annotation { "Feature Type Name" : "Feature", "Feature Type Description" : "" }
export const myFeature = defineFeature(function(context is Context, id is Id, definition is map)
    precondition{}
    {
        {
            var Q0;
            Q0=qCreatedBy(makeId("Top.planeOp"),FACE);
            var sketch = newSketch(context, id + "F0", { "sketchPlane" : qUnion([Q0])});
            skLineSegment(sketch, "E0.bottom", {"start": v(58.42, -33.26) * mm, "end": v(-58.42, -33.26) * mm});
            skLineSegment(sketch, "E0.top", {"start": v(58.42, -7.86) * mm, "end": v(-58.42, -7.86) * mm});
            skLineSegment(sketch, "E0.left", {"start": v(58.42, -33.26) * mm, "end": v(58.42, -7.86) * mm});
            skLineSegment(sketch, "E0.right", {"start": v(-58.42, -33.26) * mm, "end": v(-58.42, -7.86) * mm});
            skPoint(sketch, "E0.middle", {"position": v(0, -20.56) * mm});
            skSolve(sketch);
        }
        {
            var Q0;
            Q0=qCreatedBy(makeId("Front.planeOp"),FACE);
            var sketch = newSketch(context, id + "F1", { "sketchPlane" : qUnion([Q0])});
            skCircle(sketch, "E1", {"center": v(0, 0) * mm, "radius": 6.35 * mm});
            skCircle(sketch, "E2", {"center": v(0, 0) * mm, "radius": 7.62 * mm});
            skLineSegment(sketch, "E3", {"start": v(0, 0) * mm, "end": v(15.24, 0) * mm, "construction": true});
            skCircle(sketch, "E4", {"center": v(15.24, 0) * mm, "radius": 7.62 * mm});
            skCircle(sketch, "E5", {"center": v(15.24, 0) * mm, "radius": 6.35 * mm});
            skLineSegment(sketch, "E6", {"start": v(15.24, 0) * mm, "end": v(30.48, 0) * mm, "construction": true});
            skCircle(sketch, "E7", {"center": v(30.48, 0) * mm, "radius": 7.62 * mm});
            skCircle(sketch, "E8", {"center": v(30.48, 0) * mm, "radius": 6.35 * mm});
            skLineSegment(sketch, "E9", {"start": v(0, 0) * mm, "end": v(-15.24, 0) * mm, "construction": true});
            skCircle(sketch, "E10", {"center": v(-15.24, 0) * mm, "radius": 7.62 * mm});
            skCircle(sketch, "E11", {"center": v(-15.24, 0) * mm, "radius": 6.35 * mm});
            skLineSegment(sketch, "E12", {"start": v(-15.24, 0) * mm, "end": v(-30.48, 0) * mm, "construction": true});
            skCircle(sketch, "E13", {"center": v(-30.48, 0) * mm, "radius": 7.62 * mm});
            skCircle(sketch, "E14", {"center": v(-30.48, 0) * mm, "radius": 6.35 * mm});
            skLineSegment(sketch, "E15", {"start": v(-30.48, 0) * mm, "end": v(-45.72, 0) * mm, "construction": true});
            skCircle(sketch, "E16", {"center": v(-45.72, 0) * mm, "radius": 7.62 * mm});
            skCircle(sketch, "E17", {"center": v(-45.72, 0) * mm, "radius": 6.35 * mm});
            skLineSegment(sketch, "E18", {"start": v(30.48, 0) * mm, "end": v(45.72, 0) * mm, "construction": true});
            skCircle(sketch, "E19", {"center": v(45.72, 0) * mm, "radius": 7.62 * mm});
            skCircle(sketch, "E20", {"center": v(45.72, 0) * mm, "radius": 6.35 * mm});
            skLineSegment(sketch, "E21.bottom", {"start": v(-37.46, -1.27) * mm, "end": v(-38.73, -1.27) * mm, "construction": true});
            skLineSegment(sketch, "E21.top", {"start": v(-37.46, 1.27) * mm, "end": v(-38.73, 1.27) * mm, "construction": true});
            skLineSegment(sketch, "E21.left", {"start": v(-37.46, -1.27) * mm, "end": v(-37.46, 1.27) * mm, "construction": true});
            skLineSegment(sketch, "E21.right", {"start": v(-38.73, -1.27) * mm, "end": v(-38.73, 1.27) * mm, "construction": true});
            skPoint(sketch, "E21.middle", {"position": v(-38.1, 0) * mm});
            skLineSegment(sketch, "E22.1.0.0", {"start": v(-23.5, -1.27) * mm, "end": v(-23.5, 1.27) * mm, "construction": true});
            skLineSegment(sketch, "E22.1.0.1", {"start": v(-22.22, -1.27) * mm, "end": v(-23.5, -1.27) * mm, "construction": true});
            skLineSegment(sketch, "E22.1.0.2", {"start": v(-22.22, -1.27) * mm, "end": v(-22.22, 1.27) * mm, "construction": true});
            skLineSegment(sketch, "E22.1.0.3", {"start": v(-22.22, 1.27) * mm, "end": v(-23.5, 1.27) * mm, "construction": true});
            skLineSegment(sketch, "E22.2.0.0", {"start": v(-8.25, -1.27) * mm, "end": v(-8.25, 1.27) * mm, "construction": true});
            skLineSegment(sketch, "E22.2.0.1", {"start": v(-6.98, -1.27) * mm, "end": v(-8.25, -1.27) * mm, "construction": true});
            skLineSegment(sketch, "E22.2.0.2", {"start": v(-6.98, -1.27) * mm, "end": v(-6.98, 1.27) * mm, "construction": true});
            skLineSegment(sketch, "E22.2.0.3", {"start": v(-6.98, 1.27) * mm, "end": v(-8.25, 1.27) * mm, "construction": true});
            skLineSegment(sketch, "E22.3.0.0", {"start": v(6.99, -1.27) * mm, "end": v(6.99, 1.27) * mm, "construction": true});
            skLineSegment(sketch, "E22.3.0.1", {"start": v(8.26, -1.27) * mm, "end": v(6.99, -1.27) * mm, "construction": true});
            skLineSegment(sketch, "E22.3.0.2", {"start": v(8.26, -1.27) * mm, "end": v(8.26, 1.27) * mm, "construction": true});
            skLineSegment(sketch, "E22.3.0.3", {"start": v(8.26, 1.27) * mm, "end": v(6.99, 1.27) * mm, "construction": true});
            skLineSegment(sketch, "E22.4.0.0", {"start": v(22.23, -1.27) * mm, "end": v(22.23, 1.27) * mm, "construction": true});
            skLineSegment(sketch, "E22.4.0.1", {"start": v(23.5, -1.27) * mm, "end": v(22.23, -1.27) * mm, "construction": true});
            skLineSegment(sketch, "E22.4.0.2", {"start": v(23.5, -1.27) * mm, "end": v(23.5, 1.27) * mm, "construction": true});
            skLineSegment(sketch, "E22.4.0.3", {"start": v(23.5, 1.27) * mm, "end": v(22.23, 1.27) * mm, "construction": true});
            skLineSegment(sketch, "E22.5.0.0", {"start": v(37.47, -1.27) * mm, "end": v(37.47, 1.27) * mm, "construction": true});
            skLineSegment(sketch, "E22.5.0.1", {"start": v(38.74, -1.27) * mm, "end": v(37.47, -1.27) * mm, "construction": true});
            skLineSegment(sketch, "E22.5.0.2", {"start": v(38.74, -1.27) * mm, "end": v(38.74, 1.27) * mm, "construction": true});
            skLineSegment(sketch, "E22.5.0.3", {"start": v(38.74, 1.27) * mm, "end": v(37.47, 1.27) * mm, "construction": true});
            skSolve(sketch);
        }
        {
            var Q0;
            Q0=qCreatedBy(makeId("Front.planeOp"),FACE);
            var sketch = newSketch(context, id + "F2", { "sketchPlane" : qUnion([Q0])});
            skLineSegment(sketch, "E23", {"start": v(0, 0) * mm, "end": v(-38.1, 0) * mm, "construction": true});
            skPoint(sketch, "E24", {"position": v(-38.1, 0) * mm});
            skLineSegment(sketch, "E25.bottom", {"start": v(-37.46, -1.27) * mm, "end": v(-38.73, -1.27) * mm});
            skLineSegment(sketch, "E25.top", {"start": v(-37.46, 1.27) * mm, "end": v(-38.73, 1.27) * mm});
            skLineSegment(sketch, "E25.left", {"start": v(-37.46, -1.27) * mm, "end": v(-37.46, 1.27) * mm});
            skLineSegment(sketch, "E25.right", {"start": v(-38.73, -1.27) * mm, "end": v(-38.73, 1.27) * mm});
            skLineSegment(sketch, "E26.1.0.0", {"start": v(-22.22, 1.27) * mm, "end": v(-23.5, 1.27) * mm});
            skLineSegment(sketch, "E26.1.0.1", {"start": v(-23.5, -1.27) * mm, "end": v(-23.5, 1.27) * mm});
            skLineSegment(sketch, "E26.1.0.2", {"start": v(-22.22, -1.27) * mm, "end": v(-23.5, -1.27) * mm});
            skLineSegment(sketch, "E26.1.0.3", {"start": v(-22.22, -1.27) * mm, "end": v(-22.22, 1.27) * mm});
            skLineSegment(sketch, "E26.2.0.0", {"start": v(-6.98, 1.27) * mm, "end": v(-8.25, 1.27) * mm});
            skLineSegment(sketch, "E26.2.0.1", {"start": v(-8.25, -1.27) * mm, "end": v(-8.25, 1.27) * mm});
            skLineSegment(sketch, "E26.2.0.2", {"start": v(-6.98, -1.27) * mm, "end": v(-8.25, -1.27) * mm});
            skLineSegment(sketch, "E26.2.0.3", {"start": v(-6.98, -1.27) * mm, "end": v(-6.98, 1.27) * mm});
            skLineSegment(sketch, "E26.3.0.0", {"start": v(8.25, 1.27) * mm, "end": v(6.98, 1.27) * mm});
            skLineSegment(sketch, "E26.3.0.1", {"start": v(6.98, -1.27) * mm, "end": v(6.98, 1.27) * mm});
            skLineSegment(sketch, "E26.3.0.2", {"start": v(8.25, -1.27) * mm, "end": v(6.98, -1.27) * mm});
            skLineSegment(sketch, "E26.3.0.3", {"start": v(8.25, -1.27) * mm, "end": v(8.25, 1.27) * mm});
            skLineSegment(sketch, "E26.4.0.0", {"start": v(23.5, 1.27) * mm, "end": v(22.23, 1.27) * mm});
            skLineSegment(sketch, "E26.4.0.1", {"start": v(22.23, -1.27) * mm, "end": v(22.23, 1.27) * mm});
            skLineSegment(sketch, "E26.4.0.2", {"start": v(23.5, -1.27) * mm, "end": v(22.23, -1.27) * mm});
            skLineSegment(sketch, "E26.4.0.3", {"start": v(23.5, -1.27) * mm, "end": v(23.5, 1.27) * mm});
            skLineSegment(sketch, "E26.5.0.0", {"start": v(38.74, 1.27) * mm, "end": v(37.47, 1.27) * mm});
            skLineSegment(sketch, "E26.5.0.1", {"start": v(37.47, -1.27) * mm, "end": v(37.47, 1.27) * mm});
            skLineSegment(sketch, "E26.5.0.2", {"start": v(38.74, -1.27) * mm, "end": v(37.47, -1.27) * mm});
            skLineSegment(sketch, "E26.5.0.3", {"start": v(38.74, -1.27) * mm, "end": v(38.74, 1.27) * mm});
            skLineSegment(sketch, "E26.direction1", {"start": v(-38.73, 1.27) * mm, "end": v(-23.5, 1.27) * mm, "construction": true});
            skLineSegment(sketch, "E27", {"start": v(0, 0) * mm, "end": v(0, 6.35) * mm});
            skLineSegment(sketch, "E28", {"start": v(0, 6.35) * mm, "end": v(-47.71, 6.35) * mm});
            skSolve(sketch);
        }
        {
            var Q0;
            Q0=makeQuery(id+"F1.imprint","IMPRINT",FACE,{"disambiguationData":[TD([[makeQuery(id+"F1.imprint","IMPRINT",EDGE,{"derivedFrom":sQuery(id+"F1.wireOp",EDGE,"E17")}),-1.0]])]});
            extrude(context, id + "F3", {"entities" : qUnion([Q0]), "oppositeDirection" : true, "depth" : -152.4 * mm, "offsetDistance" : 25.4 * mm});
        }
        {
            var Q0;
            Q0 = qSketchRegion(id + "F0", true);
            extrude(context, id + "F4", {"entities" : qUnion([Q0]), "operationType" : NewBodyOperationType.ADD, "endBound" : BoundingType.SYMMETRIC, "depth" : 25.4 * mm, "offsetDistance" : 25.4 * mm});
        }
        {
            var Q0;
            Q0=makeQuery(id+"F2.imprint","IMPRINT",FACE,{"disambiguationData":[TD([[makeQuery(id+"F2.imprint","IMPRINT",EDGE,{"derivedFrom":sQuery(id+"F2.wireOp",EDGE,"E25.bottom")}),-1.0]])]});
            extrude(context, id + "F5", {"entities" : qUnion([Q0]), "operationType" : NewBodyOperationType.ADD, "depth" : 127 * mm, "offsetDistance" : 25.4 * mm});
        }
        {
            var Q0;
            Q0=makeQuery(id+"F1.imprint","IMPRINT",FACE,{"disambiguationData":[TD([[makeQuery(id+"F1.imprint","IMPRINT",EDGE,{"derivedFrom":sQuery(id+"F1.wireOp",EDGE,"E14")}),-1.0]])]});
            extrude(context, id + "F6", {"entities" : qUnion([Q0]), "operationType" : NewBodyOperationType.ADD, "depth" : 127 * mm, "offsetDistance" : 25.4 * mm});
        }
        {
            var Q0;
            Q0=makeQuery(id+"F2.imprint","IMPRINT",FACE,{"disambiguationData":[TD([[makeQuery(id+"F2.imprint","IMPRINT",EDGE,{"derivedFrom":sQuery(id+"F2.wireOp",EDGE,"E26.1.0.0")}),1.0]])]});
            extrude(context, id + "F7", {"entities" : qUnion([Q0]), "operationType" : NewBodyOperationType.ADD, "oppositeDirection" : true, "depth" : -101.6 * mm, "offsetDistance" : 25.4 * mm});
        }
        {
            var Q0;
            Q0=makeQuery(id+"F1.imprint","IMPRINT",FACE,{"disambiguationData":[TD([[makeQuery(id+"F1.imprint","IMPRINT",EDGE,{"derivedFrom":sQuery(id+"F1.wireOp",EDGE,"E11")}),-1.0]])]});
            extrude(context, id + "F8", {"entities" : qUnion([Q0]), "operationType" : NewBodyOperationType.ADD, "depth" : 101.6 * mm, "offsetDistance" : 25.4 * mm});
        }
        {
            var Q0;
            Q0=makeQuery(id+"F2.imprint","IMPRINT",FACE,{"disambiguationData":[TD([[makeQuery(id+"F2.imprint","IMPRINT",EDGE,{"derivedFrom":sQuery(id+"F2.wireOp",EDGE,"E26.2.0.0")}),1.0]])]});
            extrude(context, id + "F9", {"entities" : qUnion([Q0]), "operationType" : NewBodyOperationType.ADD, "depth" : 76.2 * mm, "offsetDistance" : 25.4 * mm});
        }
        {
            var Q0;
            Q0=makeQuery(id+"F1.imprint","IMPRINT",FACE,{"disambiguationData":[TD([[makeQuery(id+"F1.imprint","IMPRINT",EDGE,{"derivedFrom":sQuery(id+"F1.wireOp",EDGE,"E1")}),-1.0]])]});
            extrude(context, id + "F10", {"entities" : qUnion([Q0]), "operationType" : NewBodyOperationType.ADD, "depth" : 76.2 * mm, "offsetDistance" : 25.4 * mm});
        }
        {
            var Q0;
            Q0=makeQuery(id+"F2.imprint","IMPRINT",FACE,{"disambiguationData":[TD([[makeQuery(id+"F2.imprint","IMPRINT",EDGE,{"derivedFrom":sQuery(id+"F2.wireOp",EDGE,"E26.3.0.0")}),1.0]])]});
            extrude(context, id + "F11", {"entities" : qUnion([Q0]), "operationType" : NewBodyOperationType.ADD, "depth" : 63.5 * mm, "offsetDistance" : 25.4 * mm});
        }
        {
            var Q0;
            Q0=makeQuery(id+"F1.imprint","IMPRINT",FACE,{"disambiguationData":[TD([[makeQuery(id+"F1.imprint","IMPRINT",EDGE,{"derivedFrom":sQuery(id+"F1.wireOp",EDGE,"E5")}),-1.0]])]});
            extrude(context, id + "F12", {"entities" : qUnion([Q0]), "operationType" : NewBodyOperationType.ADD, "depth" : 63.5 * mm, "offsetDistance" : 25.4 * mm});
        }
        {
            var Q0;
            Q0=makeQuery(id+"F2.imprint","IMPRINT",FACE,{"disambiguationData":[TD([[makeQuery(id+"F2.imprint","IMPRINT",EDGE,{"derivedFrom":sQuery(id+"F2.wireOp",EDGE,"E26.4.0.0")}),1.0]])]});
            extrude(context, id + "F13", {"entities" : qUnion([Q0]), "operationType" : NewBodyOperationType.ADD, "depth" : 50.8 * mm, "offsetDistance" : 25.4 * mm});
        }
        {
            var Q0;
            Q0=makeQuery(id+"F1.imprint","IMPRINT",FACE,{"disambiguationData":[TD([[makeQuery(id+"F1.imprint","IMPRINT",EDGE,{"derivedFrom":sQuery(id+"F1.wireOp",EDGE,"E8")}),-1.0]])]});
            extrude(context, id + "F14", {"entities" : qUnion([Q0]), "operationType" : NewBodyOperationType.ADD, "depth" : 50.8 * mm, "offsetDistance" : 25.4 * mm});
        }
        {
            var Q0;
            Q0=makeQuery(id+"F2.imprint","IMPRINT",FACE,{"disambiguationData":[TD([[makeQuery(id+"F2.imprint","IMPRINT",EDGE,{"derivedFrom":sQuery(id+"F2.wireOp",EDGE,"E26.5.0.0")}),1.0]])]});
            extrude(context, id + "F15", {"entities" : qUnion([Q0]), "operationType" : NewBodyOperationType.ADD, "depth" : 38.1 * mm, "offsetDistance" : 25.4 * mm});
        }
        {
            var Q0;
            Q0=makeQuery(id+"F1.imprint","IMPRINT",FACE,{"disambiguationData":[TD([[makeQuery(id+"F1.imprint","IMPRINT",EDGE,{"derivedFrom":sQuery(id+"F1.wireOp",EDGE,"E20")}),-1.0]])]});
            extrude(context, id + "F16", {"entities" : qUnion([Q0]), "operationType" : NewBodyOperationType.ADD, "depth" : 38.1 * mm, "offsetDistance" : 25.4 * mm});
        }
        {
            var Q0;
            Q0=makeQuery(id+"F4.boolean.opBoolean","SPLIT",FACE,{"disambiguationData":[TD([makeQuery(id+"F3.opExtrude","SWEPT_FACE",FACE,{"disambiguationData":[OSD([sQuery(id+"F1.wireOp",EDGE,"E17")])]})])],"derivedFrom":makeQuery(id+"F4.opExtrude","SWEPT_FACE",FACE,{"disambiguationData":[OSD([sQuery(id+"F0.wireOp",EDGE,"E0.top")])]})});
            var Q1;
            {var subQ2=sQuery(id+"F0.wireOp",EDGE,"E0.top");Q1=makeQuery(id+"F6.boolean.opBoolean","SPLIT",FACE,{"disambiguationData":[TD([makeQuery(id+"F6.opExtrude","SWEPT_FACE",FACE,{"disambiguationData":[OSD([sQuery(id+"F1.wireOp",EDGE,"E14")])]})])],"derivedFrom":makeQuery(id+"F4.boolean.opBoolean","SPLIT",FACE,{"disambiguationData":[TD([makeQuery(id+"F3.opExtrude","SWEPT_FACE",FACE,{"disambiguationData":[OSD([sQuery(id+"F1.wireOp",EDGE,"E16")])]})])],"derivedFrom":makeQuery(id+"F4.opExtrude","SWEPT_FACE",FACE,{"disambiguationData":[OSD([subQ2])]})})});}
            var Q2;
            {var subQ2=sQuery(id+"F0.wireOp",EDGE,"E0.top");var subQ7=makeQuery(id+"F3.opExtrude","SWEPT_FACE",FACE,{"disambiguationData":[OSD([sQuery(id+"F1.wireOp",EDGE,"E16")])]});Q2=makeQuery(id+"F8.boolean.opBoolean","SPLIT",FACE,{"disambiguationData":[TD([makeQuery(id+"F8.opExtrude","SWEPT_FACE",FACE,{"disambiguationData":[OSD([sQuery(id+"F1.wireOp",EDGE,"E11")])]})])],"derivedFrom":makeQuery(id+"F6.boolean.opBoolean","SPLIT",FACE,{"disambiguationData":[TD([subQ7])],"derivedFrom":makeQuery(id+"F4.boolean.opBoolean","SPLIT",FACE,{"disambiguationData":[TD([subQ7])],"derivedFrom":makeQuery(id+"F4.opExtrude","SWEPT_FACE",FACE,{"disambiguationData":[OSD([subQ2])]})})})});}
            var Q3;
            {var subQ5=makeQuery(id+"F3.opExtrude","SWEPT_FACE",FACE,{"disambiguationData":[OSD([sQuery(id+"F1.wireOp",EDGE,"E16")])]});var subQ8=sQuery(id+"F0.wireOp",EDGE,"E0.top");Q3=makeQuery(id+"F10.boolean.opBoolean","SPLIT",FACE,{"disambiguationData":[TD([makeQuery(id+"F10.opExtrude","SWEPT_FACE",FACE,{"disambiguationData":[OSD([sQuery(id+"F1.wireOp",EDGE,"E1")])]})])],"derivedFrom":makeQuery(id+"F8.boolean.opBoolean","SPLIT",FACE,{"disambiguationData":[TD([subQ5])],"derivedFrom":makeQuery(id+"F6.boolean.opBoolean","SPLIT",FACE,{"disambiguationData":[TD([subQ5])],"derivedFrom":makeQuery(id+"F4.boolean.opBoolean","SPLIT",FACE,{"disambiguationData":[TD([subQ5])],"derivedFrom":makeQuery(id+"F4.opExtrude","SWEPT_FACE",FACE,{"disambiguationData":[OSD([subQ8])]})})})})});}
            var Q4;
            {var subQ6=makeQuery(id+"F3.opExtrude","SWEPT_FACE",FACE,{"disambiguationData":[OSD([sQuery(id+"F1.wireOp",EDGE,"E16")])]});var subQ9=sQuery(id+"F0.wireOp",EDGE,"E0.top");Q4=makeQuery(id+"F12.boolean.opBoolean","SPLIT",FACE,{"disambiguationData":[TD([makeQuery(id+"F12.opExtrude","SWEPT_FACE",FACE,{"disambiguationData":[OSD([sQuery(id+"F1.wireOp",EDGE,"E5")])]})])],"derivedFrom":makeQuery(id+"F10.boolean.opBoolean","SPLIT",FACE,{"disambiguationData":[TD([subQ6])],"derivedFrom":makeQuery(id+"F8.boolean.opBoolean","SPLIT",FACE,{"disambiguationData":[TD([subQ6])],"derivedFrom":makeQuery(id+"F6.boolean.opBoolean","SPLIT",FACE,{"disambiguationData":[TD([subQ6])],"derivedFrom":makeQuery(id+"F4.boolean.opBoolean","SPLIT",FACE,{"disambiguationData":[TD([subQ6])],"derivedFrom":makeQuery(id+"F4.opExtrude","SWEPT_FACE",FACE,{"disambiguationData":[OSD([subQ9])]})})})})})});}
            var Q5;
            {var subQ7=makeQuery(id+"F3.opExtrude","SWEPT_FACE",FACE,{"disambiguationData":[OSD([sQuery(id+"F1.wireOp",EDGE,"E16")])]});var subQ10=sQuery(id+"F0.wireOp",EDGE,"E0.top");Q5=makeQuery(id+"F14.boolean.opBoolean","SPLIT",FACE,{"disambiguationData":[TD([makeQuery(id+"F14.opExtrude","SWEPT_FACE",FACE,{"disambiguationData":[OSD([sQuery(id+"F1.wireOp",EDGE,"E8")])]})])],"derivedFrom":makeQuery(id+"F12.boolean.opBoolean","SPLIT",FACE,{"disambiguationData":[TD([subQ7])],"derivedFrom":makeQuery(id+"F10.boolean.opBoolean","SPLIT",FACE,{"disambiguationData":[TD([subQ7])],"derivedFrom":makeQuery(id+"F8.boolean.opBoolean","SPLIT",FACE,{"disambiguationData":[TD([subQ7])],"derivedFrom":makeQuery(id+"F6.boolean.opBoolean","SPLIT",FACE,{"disambiguationData":[TD([subQ7])],"derivedFrom":makeQuery(id+"F4.boolean.opBoolean","SPLIT",FACE,{"disambiguationData":[TD([subQ7])],"derivedFrom":makeQuery(id+"F4.opExtrude","SWEPT_FACE",FACE,{"disambiguationData":[OSD([subQ10])]})})})})})})});}
            var Q6;
            {var subQ7=makeQuery(id+"F3.opExtrude","SWEPT_FACE",FACE,{"disambiguationData":[OSD([sQuery(id+"F1.wireOp",EDGE,"E16")])]});var subQ10=sQuery(id+"F0.wireOp",EDGE,"E0.top");Q6=makeQuery(id+"F16.boolean.opBoolean","SPLIT",FACE,{"disambiguationData":[TD([makeQuery(id+"F16.opExtrude","SWEPT_FACE",FACE,{"disambiguationData":[OSD([sQuery(id+"F1.wireOp",EDGE,"E20")])]})])],"derivedFrom":makeQuery(id+"F14.boolean.opBoolean","SPLIT",FACE,{"disambiguationData":[TD([subQ7])],"derivedFrom":makeQuery(id+"F12.boolean.opBoolean","SPLIT",FACE,{"disambiguationData":[TD([subQ7])],"derivedFrom":makeQuery(id+"F10.boolean.opBoolean","SPLIT",FACE,{"disambiguationData":[TD([subQ7])],"derivedFrom":makeQuery(id+"F8.boolean.opBoolean","SPLIT",FACE,{"disambiguationData":[TD([subQ7])],"derivedFrom":makeQuery(id+"F6.boolean.opBoolean","SPLIT",FACE,{"disambiguationData":[TD([subQ7])],"derivedFrom":makeQuery(id+"F4.boolean.opBoolean","SPLIT",FACE,{"disambiguationData":[TD([subQ7])],"derivedFrom":makeQuery(id+"F4.opExtrude","SWEPT_FACE",FACE,{"disambiguationData":[OSD([subQ10])]})})})})})})})});}
            extrude(context, id + "F17", {"entities" : qUnion([Q0, Q1, Q2, Q3, Q4, Q5, Q6]), "operationType" : NewBodyOperationType.REMOVE, "oppositeDirection" : true, "depth" : 152.4 * mm, "offsetDistance" : 25.4 * mm});
        }
        {
            var Q0;
            Q0=makeQuery(id+"F4.opExtrude","CAP_FACE",FACE,{"disambiguationData":[OSD([sQuery(id+"F0.wireOp",EDGE,"E0.bottom"),sQuery(id+"F0.wireOp",EDGE,"E0.top"),sQuery(id+"F0.wireOp",EDGE,"E0.left"),sQuery(id+"F0.wireOp",EDGE,"E0.right")])],"isStart":false});
            var sketch = newSketch(context, id + "F18", { "sketchPlane" : qUnion([Q0])});
            skLineSegment(sketch, "E29.bottom", {"start": v(53.34, -26.94) * mm, "end": v(-53.34, -26.94) * mm});
            skLineSegment(sketch, "E29.top", {"start": v(53.34, -14.18) * mm, "end": v(-53.34, -14.18) * mm});
            skLineSegment(sketch, "E29.left", {"start": v(53.34, -26.94) * mm, "end": v(53.34, -14.18) * mm});
            skLineSegment(sketch, "E29.right", {"start": v(-53.34, -26.94) * mm, "end": v(-53.34, -14.18) * mm});
            skPoint(sketch, "E29.middle", {"position": v(0, -20.56) * mm});
            skText(sketch, "E30", { "text": "Jake Powers", "fontName": "RobotoSlab-Regular.ttf"});
            const initialGuessF18  = {"E30": [-0.05334, -0.02694, 1, 0, 0.01275]};
            skSetInitialGuess(sketch, initialGuessF18);
            skSolve(sketch);
        }
        {
            var Q0;
            Q0=makeQuery(id+"F18.imprint","IMPRINT",FACE,{"disambiguationData":[TD([[makeQuery(id+"F18.imprint","IMPRINT",EDGE,{"derivedFrom":sQuery(id+"F18.wireOp",EDGE,"E30.sketch_text.stroke-0")}),-1.0]])]});
            var Q1;
            Q1=makeQuery(id+"F18.imprint","IMPRINT",FACE,{"disambiguationData":[TD([[makeQuery(id+"F18.imprint","IMPRINT",EDGE,{"derivedFrom":sQuery(id+"F18.wireOp",EDGE,"E30.sketch_text.stroke-18")}),-1.0]])]});
            var Q2;
            {var subQ0=sQuery(id+"F18.wireOp",EDGE,"E30.sketch_text.stroke-56");Q2=makeQuery(id+"F18.imprint","IMPRINT",FACE,{"disambiguationData":[TD([[makeQuery(id+"F18.imprint","IMPRINT",EDGE,{"derivedFrom":subQ0}),-1.0]])]});}
            var Q3;
            {var subQ4=sQuery(id+"F18.wireOp",EDGE,"E30.sketch_text.stroke-81");Q3=makeQuery(id+"F18.imprint","IMPRINT",FACE,{"disambiguationData":[TD([[makeQuery(id+"F18.imprint","IMPRINT",EDGE,{"derivedFrom":subQ4}),-1.0]])]});}
            var Q4;
            Q4=makeQuery(id+"F18.imprint","IMPRINT",FACE,{"disambiguationData":[TD([[makeQuery(id+"F18.imprint","IMPRINT",EDGE,{"derivedFrom":sQuery(id+"F18.wireOp",EDGE,"E30.sketch_text.stroke-104")}),-1.0]])]});
            var Q5;
            Q5=makeQuery(id+"F18.imprint","IMPRINT",FACE,{"disambiguationData":[TD([[makeQuery(id+"F18.imprint","IMPRINT",EDGE,{"derivedFrom":sQuery(id+"F18.wireOp",EDGE,"E30.sketch_text.stroke-127")}),-1.0]])]});
            var Q6;
            Q6=makeQuery(id+"F18.imprint","IMPRINT",FACE,{"disambiguationData":[TD([[makeQuery(id+"F18.imprint","IMPRINT",EDGE,{"derivedFrom":sQuery(id+"F18.wireOp",EDGE,"E30.sketch_text.stroke-147")}),-1.0]])]});
            var Q7;
            {var subQ4=sQuery(id+"F18.wireOp",EDGE,"E30.sketch_text.stroke-178");Q7=makeQuery(id+"F18.imprint","IMPRINT",FACE,{"disambiguationData":[TD([[makeQuery(id+"F18.imprint","IMPRINT",EDGE,{"derivedFrom":subQ4}),-1.0]])]});}
            var Q8;
            Q8=makeQuery(id+"F18.imprint","IMPRINT",FACE,{"disambiguationData":[TD([[makeQuery(id+"F18.imprint","IMPRINT",EDGE,{"derivedFrom":sQuery(id+"F18.wireOp",EDGE,"E30.sketch_text.stroke-201")}),-1.0]])]});
            var Q9;
            Q9=makeQuery(id+"F18.imprint","IMPRINT",FACE,{"disambiguationData":[TD([[makeQuery(id+"F18.imprint","IMPRINT",EDGE,{"derivedFrom":sQuery(id+"F18.wireOp",EDGE,"E30.sketch_text.stroke-220")}),-1.0]])]});
            extrude(context, id + "F19", {"entities" : qUnion([Q0, Q1, Q2, Q3, Q4, Q5, Q6, Q7, Q8, Q9]), "operationType" : NewBodyOperationType.REMOVE, "oppositeDirection" : true, "depth" : 2.54 * mm, "offsetDistance" : 25.4 * mm});
        }
        {
            var Q0;
            Q0=makeQuery(id+"F4.opExtrude","CAP_EDGE",EDGE,{"disambiguationData":[OSD([sQuery(id+"F0.wireOp",EDGE,"E0.left")])],"isStart":true});
            var Q1;
            Q1=makeQuery(id+"F4.opExtrude","CAP_EDGE",EDGE,{"disambiguationData":[OSD([sQuery(id+"F0.wireOp",EDGE,"E0.left")])],"isStart":false});
            var Q2;
            Q2=makeQuery(id+"F4.opExtrude","CAP_EDGE",EDGE,{"disambiguationData":[OSD([sQuery(id+"F0.wireOp",EDGE,"E0.right")])],"isStart":true});
            var Q3;
            Q3=makeQuery(id+"F4.opExtrude","CAP_EDGE",EDGE,{"disambiguationData":[OSD([sQuery(id+"F0.wireOp",EDGE,"E0.right")])],"isStart":false});
            fillet(context, id + "F20", {"entities" : qUnion([Q0, Q1, Q2, Q3]), "radius" : 5.08 * mm, "tangentPropagation" : true, "allowEdgeOverflow" : false});
        }
    });